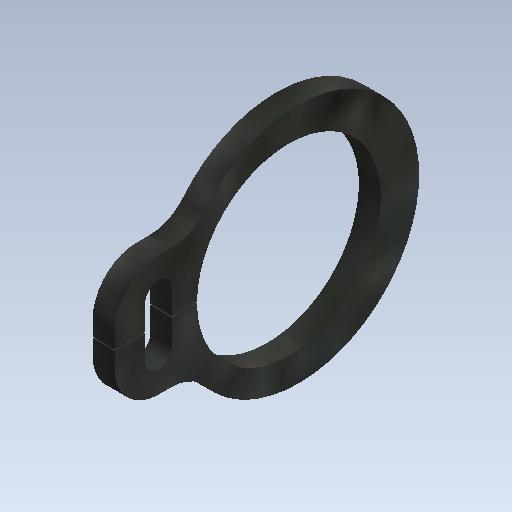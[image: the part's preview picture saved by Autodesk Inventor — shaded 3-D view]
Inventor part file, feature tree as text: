
AUTODESK INVENTOR PART (.ipt)
format: ipt  version: 2021 (Build 250183000, 183)  size: 144,384 bytes
history: native  units: mm (DEFAULTED — no unit token found)
features: other x14, extrude x1, sketch x1
ambient origin geometry x8: Origin, YZ Plane, XZ Plane, XY Plane, X Axis, Y Axis, Z Axis, Center Point
bodies: Solid1 (feature_tree)
feature tree (16):
  extrude  "Extrusion1"  TaperAngle=0.0deg  [1 undecoded]
  other  "1_XY"
  other  "1_YZ"
  other  "1_ZX"
  other  "1_X"
  other  "1_Y"
  other  "1_Z"
  other  "1_Center"
  other  "combination_module_XY"
  other  "combination_module_YZ"
  other  "combination_module_ZX"
  other  "combination_module_X"
  other  "combination_module_Y"
  other  "combination_module_Z"
  other  "combination_module_Center"
  sketch  "Sketch_5"  dims[d0=0.8mm d1=0.0mm d2=0.0mm]
note: 1 required parameter value undecoded (feature->parameter linkage not recoverable at this tier; creation-order binding heuristic only, values carry confidence <= 0.55)
